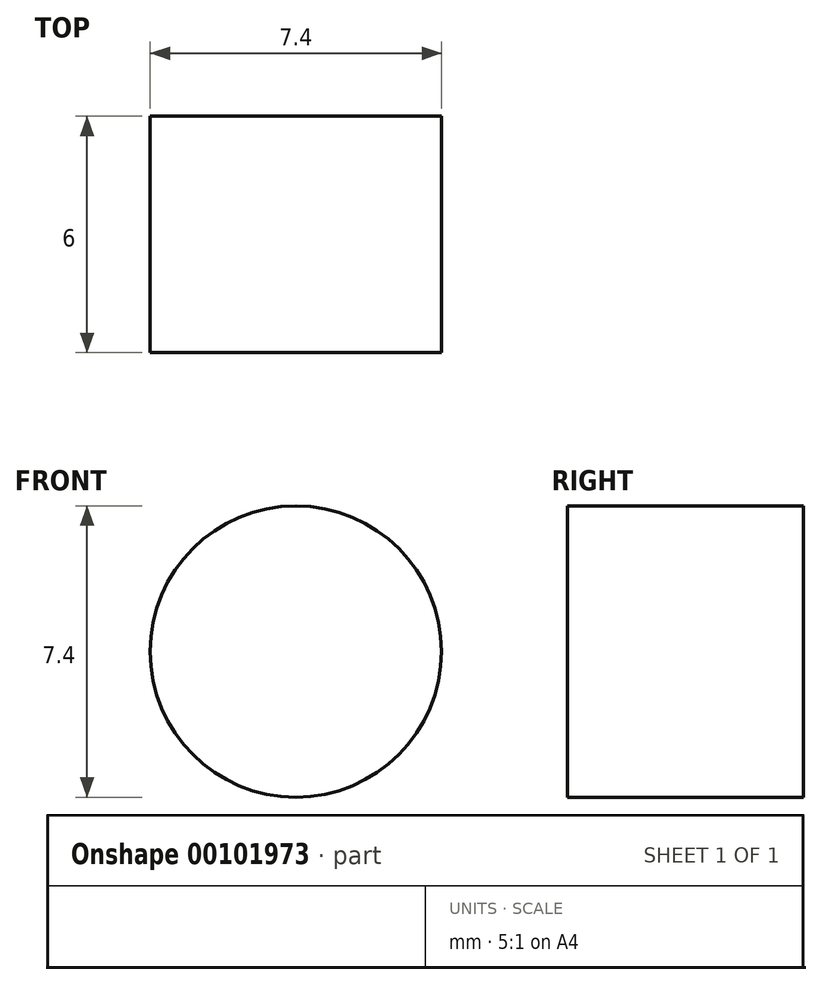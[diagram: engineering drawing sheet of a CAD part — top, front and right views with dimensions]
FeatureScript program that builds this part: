
annotation { "Feature Type Name" : "Feature", "Feature Type Description" : "" }
export const myFeature = defineFeature(function(context is Context, id is Id, definition is map)
    precondition{}
    {
        {
            var Q0;
            Q0=qCreatedBy(makeId("Front.planeOp"),FACE);
            var sketch = newSketch(context, id + "F0", { "sketchPlane" : qUnion([Q0])});
            skCircle(sketch, "E0", {"center": v(0, 0) * mm, "radius": 3.7 * mm});
            skSolve(sketch);
        }
        {
            var Q0;
            Q0=makeQuery(id+"F0.imprint","IMPRINT",FACE,{"disambiguationData":[TD([[makeQuery(id+"F0.imprint","IMPRINT",EDGE,{"derivedFrom":sQuery(id+"F0.wireOp",EDGE,"E0")}),1.0]])]});
            extrude(context, id + "F1", {"entities" : qUnion([Q0]), "depth" : 6 * mm});
        }
    });
